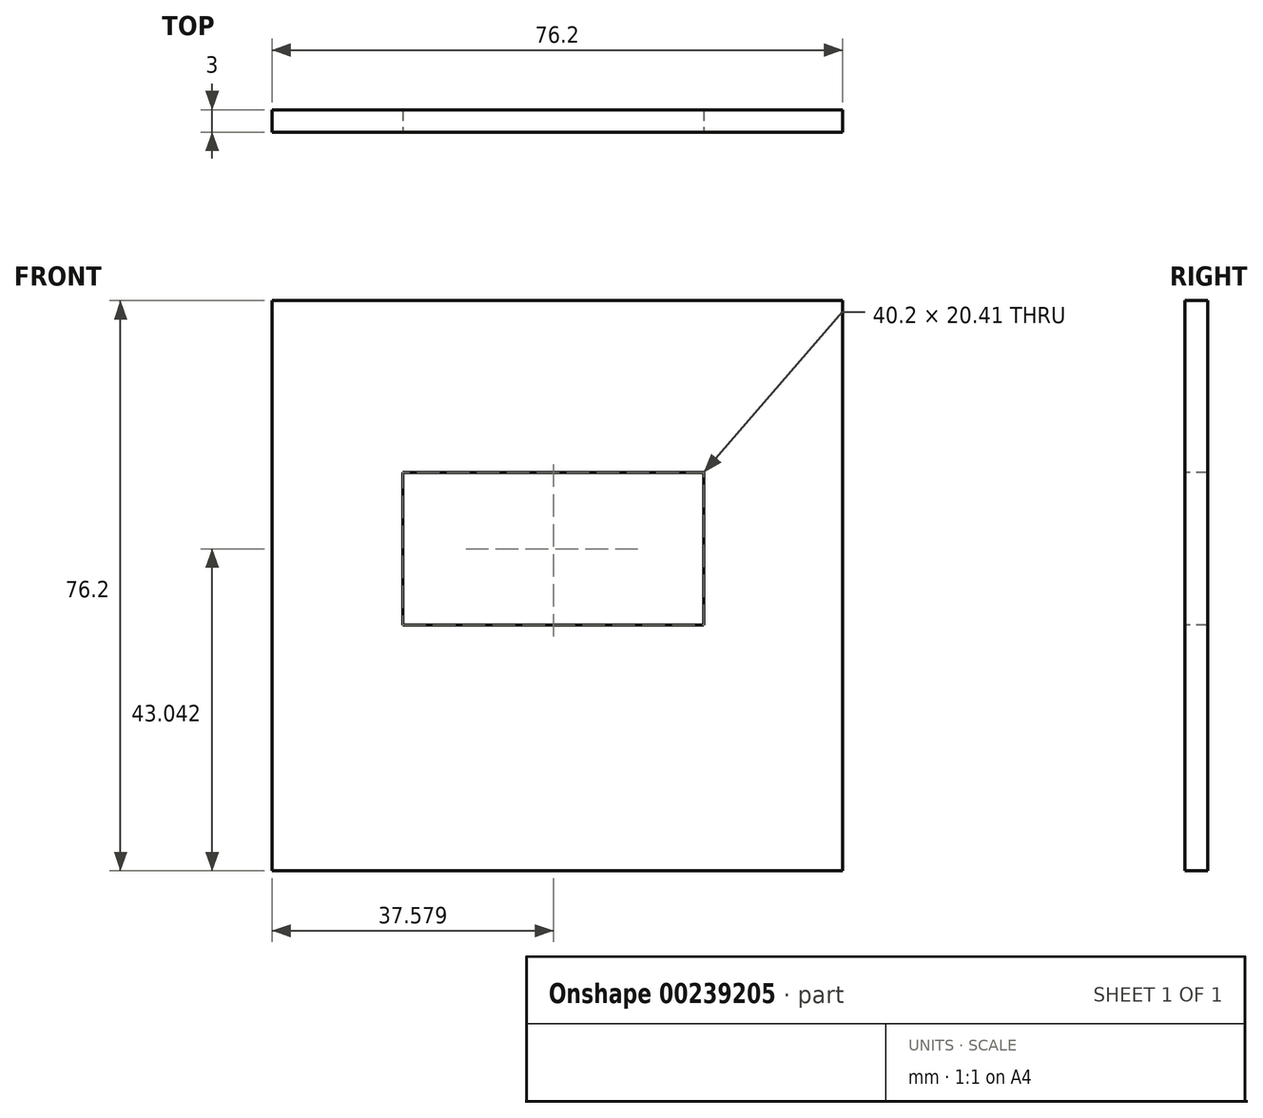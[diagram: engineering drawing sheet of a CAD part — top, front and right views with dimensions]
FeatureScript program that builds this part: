
annotation { "Feature Type Name" : "Feature", "Feature Type Description" : "" }
export const myFeature = defineFeature(function(context is Context, id is Id, definition is map)
    precondition{}
    {
        {
            assignVariable(context, id + "F0", {"name" : "A", "anyValue" : 3});
        }
        {
            var Q0;
            Q0=qCreatedBy(makeId("Front.planeOp"),FACE);
            var sketch = newSketch(context, id + "F1", { "sketchPlane" : qUnion([Q0])});
            skLineSegment(sketch, "E0.bottom", {"start": v(-38.1, 38.1) * mm, "end": v(38.1, 38.1) * mm});
            skLineSegment(sketch, "E0.top", {"start": v(-38.1, -38.1) * mm, "end": v(38.1, -38.1) * mm});
            skLineSegment(sketch, "E0.left", {"start": v(-38.1, 38.1) * mm, "end": v(-38.1, -38.1) * mm});
            skLineSegment(sketch, "E0.right", {"start": v(38.1, 38.1) * mm, "end": v(38.1, -38.1) * mm});
            skSolve(sketch);
        }
        {
            var Q0;
            Q0=makeQuery(id+"F1.imprint","IMPRINT",FACE,{"disambiguationData":[TD([[makeQuery(id+"F1.imprint","IMPRINT",EDGE,{"derivedFrom":sQuery(id+"F1.wireOp",EDGE,"E0.bottom")}),-1.0]])]});
            extrude(context, id + "F2", {"entities" : qUnion([Q0]), "endBound" : BoundingType.SYMMETRIC, "depth" : (getVariable(context, 'A')) * mm});
        }
        {
            var Q0;
            Q0=makeQuery(id+"F2.opExtrude","CAP_FACE",FACE,{"disambiguationData":[OSD([sQuery(id+"F1.wireOp",EDGE,"E0.bottom"),sQuery(id+"F1.wireOp",EDGE,"E0.top"),sQuery(id+"F1.wireOp",EDGE,"E0.left"),sQuery(id+"F1.wireOp",EDGE,"E0.right")])],"isStart":false});
            var sketch = newSketch(context, id + "F3", { "sketchPlane" : qUnion([Q0])});
            skLineSegment(sketch, "E1.bottom", {"start": v(-20.62, 15.14) * mm, "end": v(19.58, 15.14) * mm});
            skLineSegment(sketch, "E1.top", {"start": v(-20.62, -5.26) * mm, "end": v(19.58, -5.26) * mm});
            skLineSegment(sketch, "E1.left", {"start": v(-20.62, 15.14) * mm, "end": v(-20.62, -5.26) * mm});
            skLineSegment(sketch, "E1.right", {"start": v(19.58, 15.14) * mm, "end": v(19.58, -5.26) * mm});
            skSolve(sketch);
        }
        {
            var Q0;
            Q0 = qSketchRegion(id + "F3", true);
            extrude(context, id + "F4", {"entities" : qUnion([Q0]), "operationType" : NewBodyOperationType.REMOVE, "oppositeDirection" : true, "depth" : 25.4 * mm});
        }
    });
